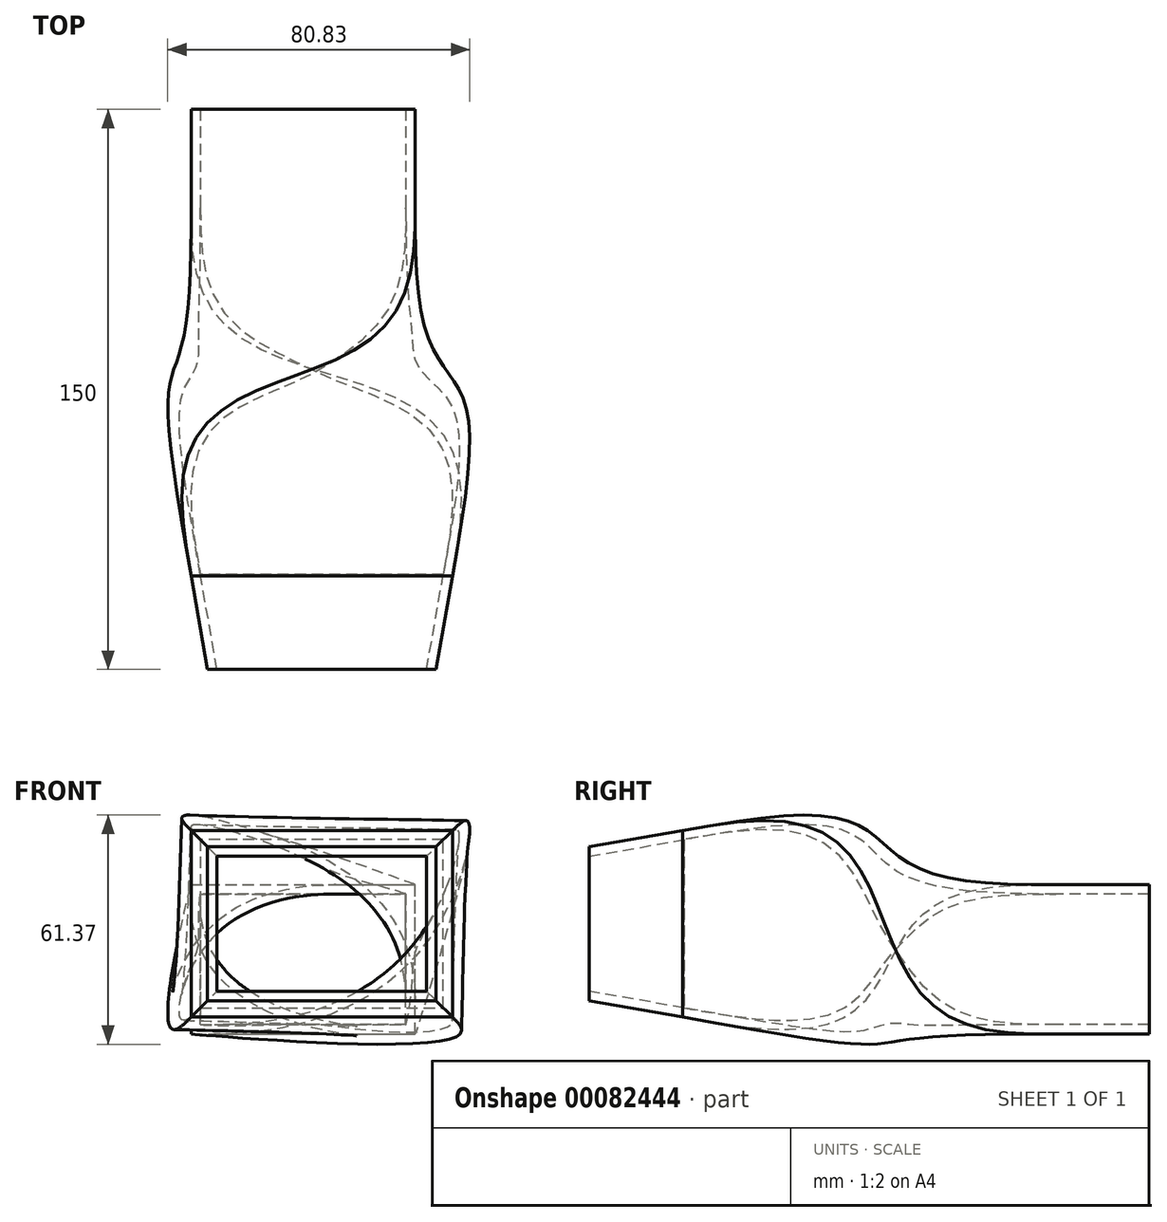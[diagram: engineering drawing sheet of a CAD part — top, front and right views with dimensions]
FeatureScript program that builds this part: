
annotation { "Feature Type Name" : "Feature", "Feature Type Description" : "" }
export const myFeature = defineFeature(function(context is Context, id is Id, definition is map)
    precondition{}
    {
        {
            var Q0;
            Q0=qCreatedBy(makeId("Front.planeOp"),FACE);
            cPlane(context, id + "F0", {"entities" : qUnion([Q0]), "cplaneType" : CPlaneType.OFFSET, "offset" : 100 * mm, "width" : 150 * mm, "height" : 150 * mm});
        }
        {
            var Q0;
            Q0=qCreatedBy(makeId("Front.planeOp"),FACE);
            var sketch = newSketch(context, id + "F1", { "sketchPlane" : qUnion([Q0])});
            skLineSegment(sketch, "E0.bottom", {"start": v(0, 0) * mm, "end": v(60, 0) * mm});
            skLineSegment(sketch, "E0.top", {"start": v(0, 40) * mm, "end": v(60, 40) * mm});
            skLineSegment(sketch, "E0.left", {"start": v(0, 0) * mm, "end": v(0, 40) * mm});
            skLineSegment(sketch, "E0.right", {"start": v(60, 0) * mm, "end": v(60, 40) * mm});
            skSolve(sketch);
        }
        {
            var Q0;
            Q0=qCreatedBy(id+"F0.planeOp",FACE);
            var sketch = newSketch(context, id + "F2", { "sketchPlane" : qUnion([Q0])});
            skLineSegment(sketch, "E1.bottom", {"start": v(0, 4.5) * mm, "end": v(70, 4.5) * mm});
            skLineSegment(sketch, "E1.top", {"start": v(0, 54.5) * mm, "end": v(70, 54.5) * mm});
            skLineSegment(sketch, "E1.left", {"start": v(0, 4.5) * mm, "end": v(0, 54.5) * mm});
            skLineSegment(sketch, "E1.right", {"start": v(70, 4.5) * mm, "end": v(70, 54.5) * mm});
            skSolve(sketch);
        }
        {
            var Q0;
            Q0=makeQuery(id+"F1.imprint","IMPRINT",FACE,{"disambiguationData":[TD([[makeQuery(id+"F1.imprint","IMPRINT",EDGE,{"derivedFrom":sQuery(id+"F1.wireOp",EDGE,"E0.bottom")}),1.0]])]});
            extrude(context, id + "F3", {"entities" : qUnion([Q0]), "oppositeDirection" : true, "depth" : 25 * mm});
        }
        {
            var Q0;
            Q0=makeQuery(id+"F2.imprint","IMPRINT",FACE,{"disambiguationData":[TD([[makeQuery(id+"F2.imprint","IMPRINT",EDGE,{"derivedFrom":sQuery(id+"F2.wireOp",EDGE,"E1.bottom")}),1.0]])]});
            extrude(context, id + "F4", {"entities" : qUnion([Q0]), "depth" : 25 * mm, "hasDraft" : true, "draftAngle" : 10 * degree, "draftPullDirection" : true});
        }
        {
            var Q0;
            Q0=makeQuery(id+"F3.opExtrude","CAP_FACE",FACE,{"disambiguationData":[OSD([sQuery(id+"F1.wireOp",EDGE,"E0.bottom"),sQuery(id+"F1.wireOp",EDGE,"E0.top"),sQuery(id+"F1.wireOp",EDGE,"E0.left"),sQuery(id+"F1.wireOp",EDGE,"E0.right")])],"isStart":true});
            var Q1;
            Q1=makeQuery(id+"F4.opExtrude","CAP_FACE",FACE,{"disambiguationData":[OSD([sQuery(id+"F2.wireOp",EDGE,"E1.bottom"),sQuery(id+"F2.wireOp",EDGE,"E1.top"),sQuery(id+"F2.wireOp",EDGE,"E1.left"),sQuery(id+"F2.wireOp",EDGE,"E1.right")])],"isStart":true});
            var Q2;
            Q2=sQuery(id+"F2.wireOp",VERTEX,"E1.left.end");
            var Q3;
            Q3=sQuery(id+"F1.wireOp",VERTEX,"E0.right.end");
            loft(context, id + "F5", {"operationType" : NewBodyOperationType.ADD, "startCondition" : LoftEndDerivativeType.MATCH_CURVATURE, "startMagnitude" : 1.5, "endCondition" : LoftEndDerivativeType.MATCH_CURVATURE, "endMagnitude" : 2, "sheetProfilesArray" : [{ "sheetProfileEntities" : qUnion([Q0]) }, { "sheetProfileEntities" : qUnion([Q1]) }], "matchConnections" : true, "connections" : [{ "connectionEntities" : qUnion([Q2, Q3]), "connectionEdgeQueries" : qUnion([]), "connectionEdgeParameters" : [] }]});
        }
        {
            var Q0;
            Q0=makeQuery(id+"F4.opExtrude","CAP_FACE",FACE,{"disambiguationData":[OSD([sQuery(id+"F2.wireOp",EDGE,"E1.bottom"),sQuery(id+"F2.wireOp",EDGE,"E1.top"),sQuery(id+"F2.wireOp",EDGE,"E1.left"),sQuery(id+"F2.wireOp",EDGE,"E1.right")])],"isStart":false});
            var Q1;
            Q1=makeQuery(id+"F3.opExtrude","CAP_FACE",FACE,{"disambiguationData":[OSD([sQuery(id+"F1.wireOp",EDGE,"E0.bottom"),sQuery(id+"F1.wireOp",EDGE,"E0.top"),sQuery(id+"F1.wireOp",EDGE,"E0.left"),sQuery(id+"F1.wireOp",EDGE,"E0.right")])],"isStart":false});
            shell(context, id + "F6", {"entities" : qUnion([Q0, Q1]), "thickness" : 2.5 * mm});
        }
    });
